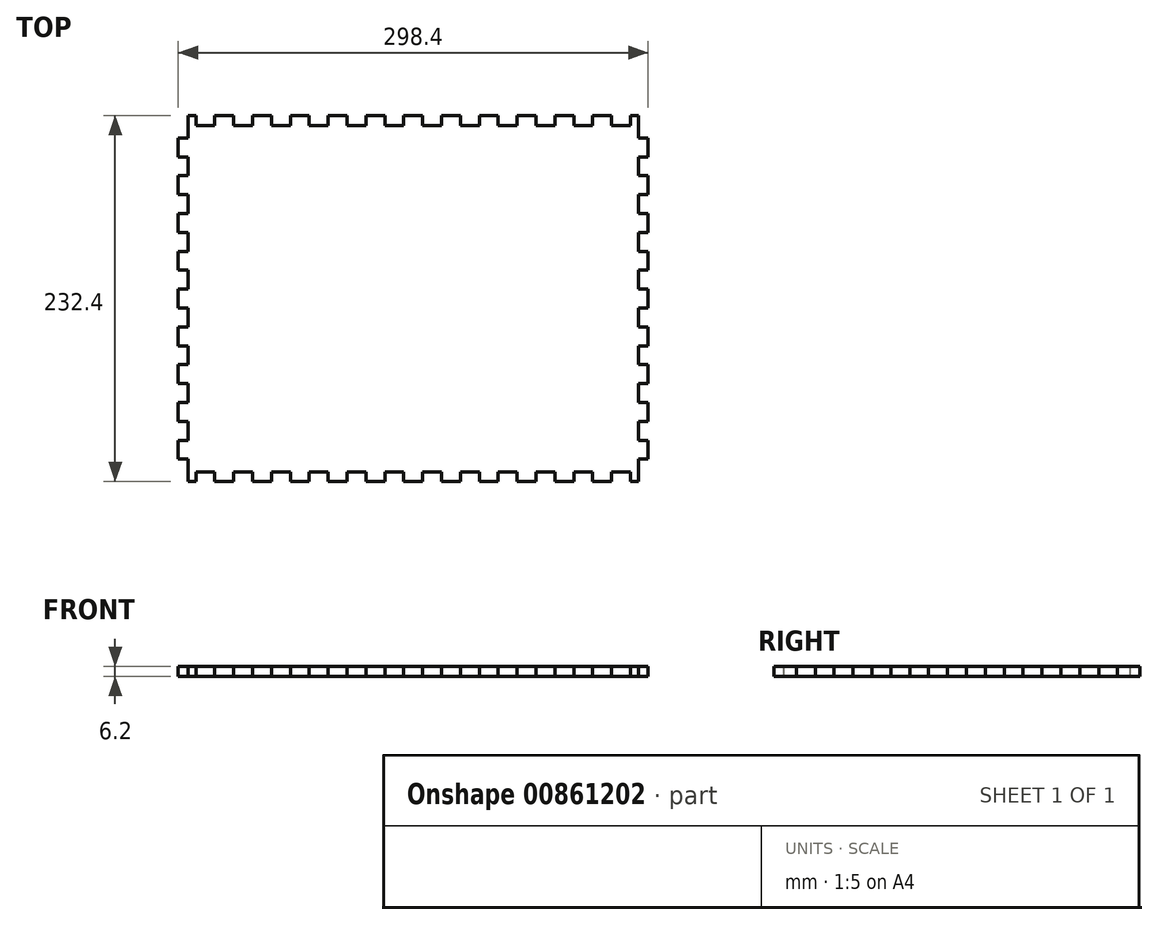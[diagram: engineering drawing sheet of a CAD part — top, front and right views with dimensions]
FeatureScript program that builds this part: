
annotation { "Feature Type Name" : "Feature", "Feature Type Description" : "" }
export const myFeature = defineFeature(function(context is Context, id is Id, definition is map)
    precondition{}
    {
        {
            var Q0;
            Q0=qCreatedBy(makeId("Top.planeOp"),FACE);
            var sketch = newSketch(context, id + "F0", { "sketchPlane" : qUnion([Q0])});
            skLineSegment(sketch, "E0.bottom", {"start": v(143, 110) * mm, "end": v(-143, 110) * mm});
            skLineSegment(sketch, "E0.top", {"start": v(143, -110) * mm, "end": v(-143, -110) * mm});
            skLineSegment(sketch, "E0.left", {"start": v(143, 110) * mm, "end": v(143, -110) * mm});
            skLineSegment(sketch, "E0.right", {"start": v(-143, 110) * mm, "end": v(-143, -110) * mm});
            skPoint(sketch, "E0.middle", {"position": v(0, 0) * mm});
            skSolve(sketch);
        }
        {
            var Q0;
            Q0 = qSketchRegion(id + "F0", true);
            extrude(context, id + "F1", {"entities" : qUnion([Q0]), "depth" : 6.2 * mm, "offsetDistance" : 25 * mm});
        }
        {
            var Q0;
            Q0=makeQuery(id+"F1.opExtrude","CAP_FACE",FACE,{"disambiguationData":[OSD([sQuery(id+"F0.wireOp",EDGE,"E0.bottom"),sQuery(id+"F0.wireOp",EDGE,"E0.top"),sQuery(id+"F0.wireOp",EDGE,"E0.left"),sQuery(id+"F0.wireOp",EDGE,"E0.right")])],"isStart":false});
            var sketch = newSketch(context, id + "F2", { "sketchPlane" : qUnion([Q0])});
            skLineSegment(sketch, "E1", {"start": v(0, 110) * mm, "end": v(0, 116.2) * mm, "construction": true});
            skLineSegment(sketch, "E2.bottom", {"start": v(6, 116.2) * mm, "end": v(-6, 116.2) * mm});
            skLineSegment(sketch, "E2.top", {"start": v(6, 110) * mm, "end": v(-6, 110) * mm});
            skLineSegment(sketch, "E2.left", {"start": v(6, 116.2) * mm, "end": v(6, 110) * mm});
            skLineSegment(sketch, "E2.right", {"start": v(-6, 116.2) * mm, "end": v(-6, 110) * mm});
            skPoint(sketch, "E2.middle", {"position": v(0, 113.1) * mm});
            skLineSegment(sketch, "E3.1.0.0", {"start": v(30, 116.2) * mm, "end": v(18, 116.2) * mm});
            skLineSegment(sketch, "E3.1.0.1", {"start": v(30, 116.2) * mm, "end": v(30, 110) * mm});
            skLineSegment(sketch, "E3.1.0.2", {"start": v(18, 116.2) * mm, "end": v(18, 110) * mm});
            skLineSegment(sketch, "E3.1.0.3", {"start": v(30, 110) * mm, "end": v(18, 110) * mm});
            skLineSegment(sketch, "E3.2.0.0", {"start": v(54, 116.2) * mm, "end": v(42, 116.2) * mm});
            skLineSegment(sketch, "E3.2.0.1", {"start": v(54, 116.2) * mm, "end": v(54, 110) * mm});
            skLineSegment(sketch, "E3.2.0.2", {"start": v(42, 116.2) * mm, "end": v(42, 110) * mm});
            skLineSegment(sketch, "E3.2.0.3", {"start": v(54, 110) * mm, "end": v(42, 110) * mm});
            skLineSegment(sketch, "E3.3.0.0", {"start": v(78, 116.2) * mm, "end": v(66, 116.2) * mm});
            skLineSegment(sketch, "E3.3.0.1", {"start": v(78, 116.2) * mm, "end": v(78, 110) * mm});
            skLineSegment(sketch, "E3.3.0.2", {"start": v(66, 116.2) * mm, "end": v(66, 110) * mm});
            skLineSegment(sketch, "E3.3.0.3", {"start": v(78, 110) * mm, "end": v(66, 110) * mm});
            skLineSegment(sketch, "E3.4.0.0", {"start": v(102, 116.2) * mm, "end": v(90, 116.2) * mm});
            skLineSegment(sketch, "E3.4.0.1", {"start": v(102, 116.2) * mm, "end": v(102, 110) * mm});
            skLineSegment(sketch, "E3.4.0.2", {"start": v(90, 116.2) * mm, "end": v(90, 110) * mm});
            skLineSegment(sketch, "E3.4.0.3", {"start": v(102, 110) * mm, "end": v(90, 110) * mm});
            skLineSegment(sketch, "E3.5.0.0", {"start": v(126, 116.2) * mm, "end": v(114, 116.2) * mm});
            skLineSegment(sketch, "E3.5.0.1", {"start": v(126, 116.2) * mm, "end": v(126, 110) * mm});
            skLineSegment(sketch, "E3.5.0.2", {"start": v(114, 116.2) * mm, "end": v(114, 110) * mm});
            skLineSegment(sketch, "E3.5.0.3", {"start": v(126, 110) * mm, "end": v(114, 110) * mm});
            skLineSegment(sketch, "E3.6.0.0", {"start": v(143, 116.2) * mm, "end": v(138, 116.2) * mm});
            skLineSegment(sketch, "E3.6.0.2", {"start": v(138, 116.2) * mm, "end": v(138, 110) * mm});
            skLineSegment(sketch, "E3.6.0.3", {"start": v(143, 110) * mm, "end": v(138, 110) * mm});
            skLineSegment(sketch, "E3.direction1", {"start": v(-6, 116.2) * mm, "end": v(18, 116.2) * mm, "construction": true});
            skLineSegment(sketch, "E4", {"start": v(143, 110) * mm, "end": v(143, 116.2) * mm});
            skPoint(sketch, "E5.orphan", {"position": v(150, 110) * mm});
            skLineSegment(sketch, "E6.MirrorCS", {"start": v(-102, 110) * mm, "end": v(-90, 110) * mm});
            skLineSegment(sketch, "E7.MirrorCS", {"start": v(-143, 116.2) * mm, "end": v(-138, 116.2) * mm});
            skLineSegment(sketch, "E8.MirrorCS", {"start": v(-138, 116.2) * mm, "end": v(-138, 110) * mm});
            skLineSegment(sketch, "E9.MirrorCS", {"start": v(-30, 116.2) * mm, "end": v(-30, 110) * mm});
            skLineSegment(sketch, "E10.MirrorCS", {"start": v(-66, 116.2) * mm, "end": v(-66, 110) * mm});
            skLineSegment(sketch, "E11.MirrorCS", {"start": v(-126, 116.2) * mm, "end": v(-126, 110) * mm});
            skLineSegment(sketch, "E12.MirrorCS", {"start": v(-54, 110) * mm, "end": v(-42, 110) * mm});
            skLineSegment(sketch, "E13.MirrorCS", {"start": v(-143, 110) * mm, "end": v(-143, 116.2) * mm});
            skLineSegment(sketch, "E14.MirrorCS", {"start": v(-54, 116.2) * mm, "end": v(-54, 110) * mm});
            skLineSegment(sketch, "E15.MirrorCS", {"start": v(-114, 116.2) * mm, "end": v(-114, 110) * mm});
            skLineSegment(sketch, "E16.MirrorCS", {"start": v(-102, 116.2) * mm, "end": v(-90, 116.2) * mm});
            skLineSegment(sketch, "E17.MirrorCS", {"start": v(-102, 116.2) * mm, "end": v(-102, 110) * mm});
            skLineSegment(sketch, "E18.MirrorCS", {"start": v(-42, 116.2) * mm, "end": v(-42, 110) * mm});
            skLineSegment(sketch, "E19.MirrorCS", {"start": v(-54, 116.2) * mm, "end": v(-42, 116.2) * mm});
            skLineSegment(sketch, "E20.MirrorCS", {"start": v(-143, 110) * mm, "end": v(-138, 110) * mm});
            skLineSegment(sketch, "E21.MirrorCS", {"start": v(-90, 116.2) * mm, "end": v(-90, 110) * mm});
            skLineSegment(sketch, "E22.MirrorCS", {"start": v(-78, 116.2) * mm, "end": v(-78, 110) * mm});
            skLineSegment(sketch, "E23.MirrorCS", {"start": v(-78, 110) * mm, "end": v(-66, 110) * mm});
            skLineSegment(sketch, "E24.MirrorCS", {"start": v(-126, 116.2) * mm, "end": v(-114, 116.2) * mm});
            skLineSegment(sketch, "E25.MirrorCS", {"start": v(-78, 116.2) * mm, "end": v(-66, 116.2) * mm});
            skLineSegment(sketch, "E26.MirrorCS", {"start": v(-126, 110) * mm, "end": v(-114, 110) * mm});
            skLineSegment(sketch, "E27.MirrorCS", {"start": v(-30, 110) * mm, "end": v(-18, 110) * mm});
            skPoint(sketch, "E28.MirrorP", {"position": v(-150, 110) * mm});
            skLineSegment(sketch, "E29.MirrorCS", {"start": v(-30, 116.2) * mm, "end": v(-18, 116.2) * mm});
            skLineSegment(sketch, "E30.MirrorCS", {"start": v(-18, 116.2) * mm, "end": v(-18, 110) * mm});
            skLineSegment(sketch, "E31.MirrorCS", {"start": v(6, -116.2) * mm, "end": v(-6, -116.2) * mm});
            skLineSegment(sketch, "E32.MirrorCS", {"start": v(-143, -116.2) * mm, "end": v(-138, -116.2) * mm});
            skLineSegment(sketch, "E33.MirrorCS", {"start": v(143, -110) * mm, "end": v(138, -110) * mm});
            skLineSegment(sketch, "E34.MirrorCS", {"start": v(-30, -116.2) * mm, "end": v(-30, -110) * mm});
            skLineSegment(sketch, "E35.MirrorCS", {"start": v(-143, -110) * mm, "end": v(-143, -116.2) * mm});
            skLineSegment(sketch, "E36.MirrorCS", {"start": v(-6, -116.2) * mm, "end": v(18, -116.2) * mm, "construction": true});
            skLineSegment(sketch, "E37.MirrorCS", {"start": v(-42, -116.2) * mm, "end": v(-42, -110) * mm});
            skLineSegment(sketch, "E38.MirrorCS", {"start": v(143, -110) * mm, "end": v(143, -116.2) * mm});
            skLineSegment(sketch, "E39.MirrorCS", {"start": v(-143, -110) * mm, "end": v(-138, -110) * mm});
            skLineSegment(sketch, "E40.MirrorCS", {"start": v(18, -116.2) * mm, "end": v(18, -110) * mm});
            skLineSegment(sketch, "E41.MirrorCS", {"start": v(-138, -116.2) * mm, "end": v(-138, -110) * mm});
            skLineSegment(sketch, "E42.MirrorCS", {"start": v(0, -110) * mm, "end": v(0, -116.2) * mm, "construction": true});
            skLineSegment(sketch, "E43.MirrorCS", {"start": v(-6, -116.2) * mm, "end": v(-6, -110) * mm});
            skLineSegment(sketch, "E44.MirrorCS", {"start": v(-54, -116.2) * mm, "end": v(-42, -116.2) * mm});
            skLineSegment(sketch, "E45.MirrorCS", {"start": v(6, -116.2) * mm, "end": v(6, -110) * mm});
            skLineSegment(sketch, "E46.MirrorCS", {"start": v(138, -116.2) * mm, "end": v(138, -110) * mm});
            skLineSegment(sketch, "E47.MirrorCS", {"start": v(6, -110) * mm, "end": v(-6, -110) * mm});
            skLineSegment(sketch, "E48.MirrorCS", {"start": v(143, -116.2) * mm, "end": v(138, -116.2) * mm});
            skLineSegment(sketch, "E49.MirrorCS", {"start": v(-30, -116.2) * mm, "end": v(-18, -116.2) * mm});
            skLineSegment(sketch, "E50.MirrorCS", {"start": v(-126, -116.2) * mm, "end": v(-126, -110) * mm});
            skLineSegment(sketch, "E51.MirrorCS", {"start": v(-102, -116.2) * mm, "end": v(-90, -116.2) * mm});
            skLineSegment(sketch, "E52.MirrorCS", {"start": v(126, -116.2) * mm, "end": v(114, -116.2) * mm});
            skLineSegment(sketch, "E53.MirrorCS", {"start": v(102, -116.2) * mm, "end": v(90, -116.2) * mm});
            skLineSegment(sketch, "E54.MirrorCS", {"start": v(126, -116.2) * mm, "end": v(126, -110) * mm});
            skLineSegment(sketch, "E55.MirrorCS", {"start": v(126, -110) * mm, "end": v(114, -110) * mm});
            skLineSegment(sketch, "E56.MirrorCS", {"start": v(78, -116.2) * mm, "end": v(66, -116.2) * mm});
            skLineSegment(sketch, "E57.MirrorCS", {"start": v(30, -110) * mm, "end": v(18, -110) * mm});
            skLineSegment(sketch, "E58.MirrorCS", {"start": v(-126, -116.2) * mm, "end": v(-114, -116.2) * mm});
            skLineSegment(sketch, "E59.MirrorCS", {"start": v(-18, -116.2) * mm, "end": v(-18, -110) * mm});
            skLineSegment(sketch, "E60.MirrorCS", {"start": v(54, -116.2) * mm, "end": v(42, -116.2) * mm});
            skLineSegment(sketch, "E61.MirrorCS", {"start": v(30, -116.2) * mm, "end": v(18, -116.2) * mm});
            skLineSegment(sketch, "E62.MirrorCS", {"start": v(54, -116.2) * mm, "end": v(54, -110) * mm});
            skLineSegment(sketch, "E63.MirrorCS", {"start": v(54, -110) * mm, "end": v(42, -110) * mm});
            skLineSegment(sketch, "E64.MirrorCS", {"start": v(-78, -116.2) * mm, "end": v(-66, -116.2) * mm});
            skLineSegment(sketch, "E65.MirrorCS", {"start": v(-30, -110) * mm, "end": v(-18, -110) * mm});
            skLineSegment(sketch, "E66.MirrorCS", {"start": v(-102, -110) * mm, "end": v(-90, -110) * mm});
            skLineSegment(sketch, "E67.MirrorCS", {"start": v(-102, -116.2) * mm, "end": v(-102, -110) * mm});
            skLineSegment(sketch, "E68.MirrorCS", {"start": v(90, -116.2) * mm, "end": v(90, -110) * mm});
            skLineSegment(sketch, "E69.MirrorCS", {"start": v(78, -110) * mm, "end": v(66, -110) * mm});
            skLineSegment(sketch, "E70.MirrorCS", {"start": v(78, -116.2) * mm, "end": v(78, -110) * mm});
            skLineSegment(sketch, "E71.MirrorCS", {"start": v(66, -116.2) * mm, "end": v(66, -110) * mm});
            skLineSegment(sketch, "E72.MirrorCS", {"start": v(102, -110) * mm, "end": v(90, -110) * mm});
            skLineSegment(sketch, "E73.MirrorCS", {"start": v(-114, -116.2) * mm, "end": v(-114, -110) * mm});
            skLineSegment(sketch, "E74.MirrorCS", {"start": v(-126, -110) * mm, "end": v(-114, -110) * mm});
            skLineSegment(sketch, "E75.MirrorCS", {"start": v(-90, -116.2) * mm, "end": v(-90, -110) * mm});
            skLineSegment(sketch, "E76.MirrorCS", {"start": v(-78, -110) * mm, "end": v(-66, -110) * mm});
            skLineSegment(sketch, "E77.MirrorCS", {"start": v(-54, -110) * mm, "end": v(-42, -110) * mm});
            skLineSegment(sketch, "E78.MirrorCS", {"start": v(114, -116.2) * mm, "end": v(114, -110) * mm});
            skLineSegment(sketch, "E79.MirrorCS", {"start": v(-54, -116.2) * mm, "end": v(-54, -110) * mm});
            skLineSegment(sketch, "E80.MirrorCS", {"start": v(-78, -116.2) * mm, "end": v(-78, -110) * mm});
            skLineSegment(sketch, "E81.MirrorCS", {"start": v(42, -116.2) * mm, "end": v(42, -110) * mm});
            skLineSegment(sketch, "E82.MirrorCS", {"start": v(102, -116.2) * mm, "end": v(102, -110) * mm});
            skLineSegment(sketch, "E83.MirrorCS", {"start": v(-66, -116.2) * mm, "end": v(-66, -110) * mm});
            skLineSegment(sketch, "E84.MirrorCS", {"start": v(30, -116.2) * mm, "end": v(30, -110) * mm});
            skPoint(sketch, "E85.MirrorP", {"position": v(-150, -110) * mm});
            skPoint(sketch, "E86.MirrorP", {"position": v(0, -113.1) * mm});
            skPoint(sketch, "E87.MirrorP", {"position": v(150, -110) * mm});
            skSolve(sketch);
        }
        {
            var Q0;
            Q0=makeQuery(id+"F2.imprint","IMPRINT",FACE,{"disambiguationData":[TD([[makeQuery(id+"F2.imprint","IMPRINT",EDGE,{"derivedFrom":sQuery(id+"F2.wireOp",EDGE,"E3.6.0.0")}),1.0]])]});
            var Q1;
            Q1=makeQuery(id+"F2.imprint","IMPRINT",FACE,{"disambiguationData":[TD([[makeQuery(id+"F2.imprint","IMPRINT",EDGE,{"derivedFrom":sQuery(id+"F2.wireOp",EDGE,"E3.5.0.0")}),1.0]])]});
            var Q2;
            Q2=makeQuery(id+"F2.imprint","IMPRINT",FACE,{"disambiguationData":[TD([[makeQuery(id+"F2.imprint","IMPRINT",EDGE,{"derivedFrom":sQuery(id+"F2.wireOp",EDGE,"E3.4.0.0")}),1.0]])]});
            var Q3;
            Q3=makeQuery(id+"F2.imprint","IMPRINT",FACE,{"disambiguationData":[TD([[makeQuery(id+"F2.imprint","IMPRINT",EDGE,{"derivedFrom":sQuery(id+"F2.wireOp",EDGE,"E3.3.0.0")}),1.0]])]});
            var Q4;
            Q4=makeQuery(id+"F2.imprint","IMPRINT",FACE,{"disambiguationData":[TD([[makeQuery(id+"F2.imprint","IMPRINT",EDGE,{"derivedFrom":sQuery(id+"F2.wireOp",EDGE,"E3.2.0.0")}),1.0]])]});
            var Q5;
            Q5=makeQuery(id+"F2.imprint","IMPRINT",FACE,{"disambiguationData":[TD([[makeQuery(id+"F2.imprint","IMPRINT",EDGE,{"derivedFrom":sQuery(id+"F2.wireOp",EDGE,"E3.1.0.0")}),1.0]])]});
            var Q6;
            Q6=makeQuery(id+"F2.imprint","IMPRINT",FACE,{"disambiguationData":[TD([[makeQuery(id+"F2.imprint","IMPRINT",EDGE,{"derivedFrom":sQuery(id+"F2.wireOp",EDGE,"E2.bottom")}),1.0]])]});
            var Q7;
            Q7=makeQuery(id+"F2.imprint","IMPRINT",FACE,{"disambiguationData":[TD([[makeQuery(id+"F2.imprint","IMPRINT",EDGE,{"derivedFrom":sQuery(id+"F2.wireOp",EDGE,"E9.MirrorCS")}),1.0]])]});
            var Q8;
            Q8=makeQuery(id+"F2.imprint","IMPRINT",FACE,{"disambiguationData":[TD([[makeQuery(id+"F2.imprint","IMPRINT",EDGE,{"derivedFrom":sQuery(id+"F2.wireOp",EDGE,"E12.MirrorCS")}),-1.0]])]});
            var Q9;
            Q9=makeQuery(id+"F2.imprint","IMPRINT",FACE,{"disambiguationData":[TD([[makeQuery(id+"F2.imprint","IMPRINT",EDGE,{"derivedFrom":sQuery(id+"F2.wireOp",EDGE,"E10.MirrorCS")}),-1.0]])]});
            var Q10;
            Q10=makeQuery(id+"F2.imprint","IMPRINT",FACE,{"disambiguationData":[TD([[makeQuery(id+"F2.imprint","IMPRINT",EDGE,{"derivedFrom":sQuery(id+"F2.wireOp",EDGE,"E6.MirrorCS")}),-1.0]])]});
            var Q11;
            Q11=makeQuery(id+"F2.imprint","IMPRINT",FACE,{"disambiguationData":[TD([[makeQuery(id+"F2.imprint","IMPRINT",EDGE,{"derivedFrom":sQuery(id+"F2.wireOp",EDGE,"E11.MirrorCS")}),1.0]])]});
            var Q12;
            Q12=makeQuery(id+"F2.imprint","IMPRINT",FACE,{"disambiguationData":[TD([[makeQuery(id+"F2.imprint","IMPRINT",EDGE,{"derivedFrom":sQuery(id+"F2.wireOp",EDGE,"E7.MirrorCS")}),-1.0]])]});
            var Q13;
            Q13=makeQuery(id+"F2.imprint","IMPRINT",FACE,{"disambiguationData":[TD([[makeQuery(id+"F2.imprint","IMPRINT",EDGE,{"derivedFrom":sQuery(id+"F2.wireOp",EDGE,"E32.MirrorCS")}),1.0]])]});
            var Q14;
            Q14=makeQuery(id+"F2.imprint","IMPRINT",FACE,{"disambiguationData":[TD([[makeQuery(id+"F2.imprint","IMPRINT",EDGE,{"derivedFrom":sQuery(id+"F2.wireOp",EDGE,"E50.MirrorCS")}),-1.0]])]});
            var Q15;
            Q15=makeQuery(id+"F2.imprint","IMPRINT",FACE,{"disambiguationData":[TD([[makeQuery(id+"F2.imprint","IMPRINT",EDGE,{"derivedFrom":sQuery(id+"F2.wireOp",EDGE,"E51.MirrorCS")}),1.0]])]});
            var Q16;
            Q16=makeQuery(id+"F2.imprint","IMPRINT",FACE,{"disambiguationData":[TD([[makeQuery(id+"F2.imprint","IMPRINT",EDGE,{"derivedFrom":sQuery(id+"F2.wireOp",EDGE,"E64.MirrorCS")}),1.0]])]});
            var Q17;
            Q17=makeQuery(id+"F2.imprint","IMPRINT",FACE,{"disambiguationData":[TD([[makeQuery(id+"F2.imprint","IMPRINT",EDGE,{"derivedFrom":sQuery(id+"F2.wireOp",EDGE,"E37.MirrorCS")}),1.0]])]});
            var Q18;
            Q18=makeQuery(id+"F2.imprint","IMPRINT",FACE,{"disambiguationData":[TD([[makeQuery(id+"F2.imprint","IMPRINT",EDGE,{"derivedFrom":sQuery(id+"F2.wireOp",EDGE,"E34.MirrorCS")}),-1.0]])]});
            var Q19;
            Q19=makeQuery(id+"F2.imprint","IMPRINT",FACE,{"disambiguationData":[TD([[makeQuery(id+"F2.imprint","IMPRINT",EDGE,{"derivedFrom":sQuery(id+"F2.wireOp",EDGE,"E31.MirrorCS")}),-1.0]])]});
            var Q20;
            Q20=makeQuery(id+"F2.imprint","IMPRINT",FACE,{"disambiguationData":[TD([[makeQuery(id+"F2.imprint","IMPRINT",EDGE,{"derivedFrom":sQuery(id+"F2.wireOp",EDGE,"E40.MirrorCS")}),-1.0]])]});
            var Q21;
            Q21=makeQuery(id+"F2.imprint","IMPRINT",FACE,{"disambiguationData":[TD([[makeQuery(id+"F2.imprint","IMPRINT",EDGE,{"derivedFrom":sQuery(id+"F2.wireOp",EDGE,"E60.MirrorCS")}),-1.0]])]});
            var Q22;
            Q22=makeQuery(id+"F2.imprint","IMPRINT",FACE,{"disambiguationData":[TD([[makeQuery(id+"F2.imprint","IMPRINT",EDGE,{"derivedFrom":sQuery(id+"F2.wireOp",EDGE,"E56.MirrorCS")}),-1.0]])]});
            var Q23;
            Q23=makeQuery(id+"F2.imprint","IMPRINT",FACE,{"disambiguationData":[TD([[makeQuery(id+"F2.imprint","IMPRINT",EDGE,{"derivedFrom":sQuery(id+"F2.wireOp",EDGE,"E53.MirrorCS")}),-1.0]])]});
            var Q24;
            Q24=makeQuery(id+"F2.imprint","IMPRINT",FACE,{"disambiguationData":[TD([[makeQuery(id+"F2.imprint","IMPRINT",EDGE,{"derivedFrom":sQuery(id+"F2.wireOp",EDGE,"E52.MirrorCS")}),-1.0]])]});
            var Q25;
            Q25=makeQuery(id+"F2.imprint","IMPRINT",FACE,{"disambiguationData":[TD([[makeQuery(id+"F2.imprint","IMPRINT",EDGE,{"derivedFrom":sQuery(id+"F2.wireOp",EDGE,"E33.MirrorCS")}),1.0]])]});
            var Q26;
            Q26=makeQuery(id+"F1.opExtrude","CAP_FACE",FACE,{"disambiguationData":[OSD([sQuery(id+"F0.wireOp",EDGE,"E0.bottom"),sQuery(id+"F0.wireOp",EDGE,"E0.top"),sQuery(id+"F0.wireOp",EDGE,"E0.left"),sQuery(id+"F0.wireOp",EDGE,"E0.right")])],"isStart":true});
            extrude(context, id + "F3", {"entities" : qUnion([Q0, Q1, Q2, Q3, Q4, Q5, Q6, Q7, Q8, Q9, Q10, Q11, Q12, Q13, Q14, Q15, Q16, Q17, Q18, Q19, Q20, Q21, Q22, Q23, Q24, Q25]), "operationType" : NewBodyOperationType.ADD, "endBound" : BoundingType.UP_TO_SURFACE, "oppositeDirection" : true, "depth" : 25 * mm, "endBoundEntityFace" : qUnion([Q26]), "offsetDistance" : 25 * mm});
        }
        {
            var Q0;
            Q0=makeQuery(id+"F3.boolean.opBoolean","MERGE",FACE,{"derivedFrom":[makeQuery(id+"F1.opExtrude","CAP_FACE",FACE,{"disambiguationData":[OSD([sQuery(id+"F0.wireOp",EDGE,"E0.bottom"),sQuery(id+"F0.wireOp",EDGE,"E0.top"),sQuery(id+"F0.wireOp",EDGE,"E0.left"),sQuery(id+"F0.wireOp",EDGE,"E0.right")])],"isStart":false}),makeQuery(id+"F3.opExtrude","CAP_FACE",FACE,{"disambiguationData":[OSD([sQuery(id+"F2.wireOp",EDGE,"E2.bottom"),sQuery(id+"F2.wireOp",EDGE,"E2.top"),sQuery(id+"F2.wireOp",EDGE,"E2.left"),sQuery(id+"F2.wireOp",EDGE,"E2.right")])],"isStart":true}),makeQuery(id+"F3.opExtrude","CAP_FACE",FACE,{"disambiguationData":[OSD([sQuery(id+"F2.wireOp",EDGE,"E3.1.0.0"),sQuery(id+"F2.wireOp",EDGE,"E3.1.0.1"),sQuery(id+"F2.wireOp",EDGE,"E3.1.0.2"),sQuery(id+"F2.wireOp",EDGE,"E3.1.0.3")])],"isStart":true}),makeQuery(id+"F3.opExtrude","CAP_FACE",FACE,{"disambiguationData":[OSD([sQuery(id+"F2.wireOp",EDGE,"E3.2.0.0"),sQuery(id+"F2.wireOp",EDGE,"E3.2.0.1"),sQuery(id+"F2.wireOp",EDGE,"E3.2.0.2"),sQuery(id+"F2.wireOp",EDGE,"E3.2.0.3")])],"isStart":true}),makeQuery(id+"F3.opExtrude","CAP_FACE",FACE,{"disambiguationData":[OSD([sQuery(id+"F2.wireOp",EDGE,"E3.3.0.0"),sQuery(id+"F2.wireOp",EDGE,"E3.3.0.1"),sQuery(id+"F2.wireOp",EDGE,"E3.3.0.2"),sQuery(id+"F2.wireOp",EDGE,"E3.3.0.3")])],"isStart":true}),makeQuery(id+"F3.opExtrude","CAP_FACE",FACE,{"disambiguationData":[OSD([sQuery(id+"F2.wireOp",EDGE,"E3.4.0.0"),sQuery(id+"F2.wireOp",EDGE,"E3.4.0.1"),sQuery(id+"F2.wireOp",EDGE,"E3.4.0.2"),sQuery(id+"F2.wireOp",EDGE,"E3.4.0.3")])],"isStart":true}),makeQuery(id+"F3.opExtrude","CAP_FACE",FACE,{"disambiguationData":[OSD([sQuery(id+"F2.wireOp",EDGE,"E3.5.0.0"),sQuery(id+"F2.wireOp",EDGE,"E3.5.0.1"),sQuery(id+"F2.wireOp",EDGE,"E3.5.0.2"),sQuery(id+"F2.wireOp",EDGE,"E3.5.0.3")])],"isStart":true}),makeQuery(id+"F3.opExtrude","CAP_FACE",FACE,{"disambiguationData":[OSD([sQuery(id+"F2.wireOp",EDGE,"E3.6.0.0"),sQuery(id+"F2.wireOp",EDGE,"E3.6.0.2"),sQuery(id+"F2.wireOp",EDGE,"E3.6.0.3"),sQuery(id+"F2.wireOp",EDGE,"E4")])],"isStart":true}),makeQuery(id+"F3.opExtrude","CAP_FACE",FACE,{"disambiguationData":[OSD([sQuery(id+"F2.wireOp",EDGE,"E6.MirrorCS"),sQuery(id+"F2.wireOp",EDGE,"E16.MirrorCS"),sQuery(id+"F2.wireOp",EDGE,"E17.MirrorCS"),sQuery(id+"F2.wireOp",EDGE,"E21.MirrorCS")])],"isStart":true}),makeQuery(id+"F3.opExtrude","CAP_FACE",FACE,{"disambiguationData":[OSD([sQuery(id+"F2.wireOp",EDGE,"E7.MirrorCS"),sQuery(id+"F2.wireOp",EDGE,"E8.MirrorCS"),sQuery(id+"F2.wireOp",EDGE,"E13.MirrorCS"),sQuery(id+"F2.wireOp",EDGE,"E20.MirrorCS")])],"isStart":true}),makeQuery(id+"F3.opExtrude","CAP_FACE",FACE,{"disambiguationData":[OSD([sQuery(id+"F2.wireOp",EDGE,"E9.MirrorCS"),sQuery(id+"F2.wireOp",EDGE,"E27.MirrorCS"),sQuery(id+"F2.wireOp",EDGE,"E29.MirrorCS"),sQuery(id+"F2.wireOp",EDGE,"E30.MirrorCS")])],"isStart":true}),makeQuery(id+"F3.opExtrude","CAP_FACE",FACE,{"disambiguationData":[OSD([sQuery(id+"F2.wireOp",EDGE,"E10.MirrorCS"),sQuery(id+"F2.wireOp",EDGE,"E22.MirrorCS"),sQuery(id+"F2.wireOp",EDGE,"E23.MirrorCS"),sQuery(id+"F2.wireOp",EDGE,"E25.MirrorCS")])],"isStart":true}),makeQuery(id+"F3.opExtrude","CAP_FACE",FACE,{"disambiguationData":[OSD([sQuery(id+"F2.wireOp",EDGE,"E11.MirrorCS"),sQuery(id+"F2.wireOp",EDGE,"E15.MirrorCS"),sQuery(id+"F2.wireOp",EDGE,"E24.MirrorCS"),sQuery(id+"F2.wireOp",EDGE,"E26.MirrorCS")])],"isStart":true}),makeQuery(id+"F3.opExtrude","CAP_FACE",FACE,{"disambiguationData":[OSD([sQuery(id+"F2.wireOp",EDGE,"E12.MirrorCS"),sQuery(id+"F2.wireOp",EDGE,"E14.MirrorCS"),sQuery(id+"F2.wireOp",EDGE,"E18.MirrorCS"),sQuery(id+"F2.wireOp",EDGE,"E19.MirrorCS")])],"isStart":true})]});
            var sketch = newSketch(context, id + "F4", { "sketchPlane" : qUnion([Q0])});
            skLineSegment(sketch, "E88", {"start": v(-138, 110) * mm, "end": v(143, 110) * mm, "construction": true});
            skLineSegment(sketch, "E89", {"start": v(0, 0) * mm, "end": v(143, 0) * mm, "construction": true});
            skLineSegment(sketch, "E90", {"start": v(143, 0) * mm, "end": v(149.2, 0) * mm, "construction": true});
            skLineSegment(sketch, "E91.bottom", {"start": v(149.2, 6) * mm, "end": v(143, 6) * mm});
            skLineSegment(sketch, "E91.top", {"start": v(149.2, -6) * mm, "end": v(143, -6) * mm});
            skLineSegment(sketch, "E91.left", {"start": v(149.2, 6) * mm, "end": v(149.2, -6) * mm});
            skLineSegment(sketch, "E91.right", {"start": v(143, 6) * mm, "end": v(143, -6) * mm});
            skPoint(sketch, "E91.middle", {"position": v(146.1, 0) * mm});
            skLineSegment(sketch, "E92.0.1.0", {"start": v(149.2, 30) * mm, "end": v(143, 30) * mm});
            skLineSegment(sketch, "E92.0.1.1", {"start": v(143, 30) * mm, "end": v(143, 18) * mm});
            skLineSegment(sketch, "E92.0.1.2", {"start": v(149.2, 30) * mm, "end": v(149.2, 18) * mm});
            skLineSegment(sketch, "E92.0.1.3", {"start": v(149.2, 18) * mm, "end": v(143, 18) * mm});
            skLineSegment(sketch, "E92.0.2.0", {"start": v(149.2, 54) * mm, "end": v(143, 54) * mm});
            skLineSegment(sketch, "E92.0.2.1", {"start": v(143, 54) * mm, "end": v(143, 42) * mm});
            skLineSegment(sketch, "E92.0.2.2", {"start": v(149.2, 54) * mm, "end": v(149.2, 42) * mm});
            skLineSegment(sketch, "E92.0.2.3", {"start": v(149.2, 42) * mm, "end": v(143, 42) * mm});
            skLineSegment(sketch, "E92.0.3.0", {"start": v(149.2, 78) * mm, "end": v(143, 78) * mm});
            skLineSegment(sketch, "E92.0.3.1", {"start": v(143, 78) * mm, "end": v(143, 66) * mm});
            skLineSegment(sketch, "E92.0.3.2", {"start": v(149.2, 78) * mm, "end": v(149.2, 66) * mm});
            skLineSegment(sketch, "E92.0.3.3", {"start": v(149.2, 66) * mm, "end": v(143, 66) * mm});
            skLineSegment(sketch, "E92.0.4.0", {"start": v(149.2, 102) * mm, "end": v(143, 102) * mm});
            skLineSegment(sketch, "E92.0.4.1", {"start": v(143, 102) * mm, "end": v(143, 90) * mm});
            skLineSegment(sketch, "E92.0.4.2", {"start": v(149.2, 102) * mm, "end": v(149.2, 90) * mm});
            skLineSegment(sketch, "E92.0.4.3", {"start": v(149.2, 90) * mm, "end": v(143, 90) * mm});
            skLineSegment(sketch, "E92.direction1", {"start": v(143, 6) * mm, "end": v(168, 6) * mm, "construction": true});
            skLineSegment(sketch, "E92.direction2", {"start": v(143, 6) * mm, "end": v(143, 30) * mm, "construction": true});
            skLineSegment(sketch, "E93.MirrorCS", {"start": v(143, -30) * mm, "end": v(143, -18) * mm});
            skLineSegment(sketch, "E94.MirrorCS", {"start": v(149.2, -78) * mm, "end": v(149.2, -66) * mm});
            skLineSegment(sketch, "E95.MirrorCS", {"start": v(149.2, -66) * mm, "end": v(143, -66) * mm});
            skLineSegment(sketch, "E96.MirrorCS", {"start": v(149.2, -102) * mm, "end": v(143, -102) * mm});
            skLineSegment(sketch, "E97.MirrorCS", {"start": v(143, -102) * mm, "end": v(143, -90) * mm});
            skLineSegment(sketch, "E98.MirrorCS", {"start": v(149.2, -102) * mm, "end": v(149.2, -90) * mm});
            skLineSegment(sketch, "E99.MirrorCS", {"start": v(149.2, -90) * mm, "end": v(143, -90) * mm});
            skLineSegment(sketch, "E100.MirrorCS", {"start": v(143, -6) * mm, "end": v(143, -30) * mm, "construction": true});
            skLineSegment(sketch, "E101.MirrorCS", {"start": v(143, -54) * mm, "end": v(143, -42) * mm});
            skLineSegment(sketch, "E102.MirrorCS", {"start": v(149.2, -42) * mm, "end": v(143, -42) * mm});
            skLineSegment(sketch, "E103.MirrorCS", {"start": v(149.2, -54) * mm, "end": v(143, -54) * mm});
            skLineSegment(sketch, "E104.MirrorCS", {"start": v(149.2, -54) * mm, "end": v(149.2, -42) * mm});
            skLineSegment(sketch, "E105.MirrorCS", {"start": v(149.2, -18) * mm, "end": v(143, -18) * mm});
            skLineSegment(sketch, "E106.MirrorCS", {"start": v(143, -78) * mm, "end": v(143, -66) * mm});
            skLineSegment(sketch, "E107.MirrorCS", {"start": v(149.2, -78) * mm, "end": v(143, -78) * mm});
            skLineSegment(sketch, "E108.MirrorCS", {"start": v(149.2, -30) * mm, "end": v(143, -30) * mm});
            skLineSegment(sketch, "E109.MirrorCS", {"start": v(149.2, -30) * mm, "end": v(149.2, -18) * mm});
            skLineSegment(sketch, "E110.MirrorCS", {"start": v(-143, 6) * mm, "end": v(-143, -6) * mm});
            skLineSegment(sketch, "E111.MirrorCS", {"start": v(-149.2, 6) * mm, "end": v(-149.2, -6) * mm});
            skLineSegment(sketch, "E112.MirrorCS", {"start": v(-149.2, -6) * mm, "end": v(-143, -6) * mm});
            skLineSegment(sketch, "E113.MirrorCS", {"start": v(-149.2, 6) * mm, "end": v(-143, 6) * mm});
            skLineSegment(sketch, "E114.MirrorCS", {"start": v(-143, 0) * mm, "end": v(-149.2, 0) * mm, "construction": true});
            skLineSegment(sketch, "E115.MirrorCS", {"start": v(-143, 30) * mm, "end": v(-143, 18) * mm});
            skLineSegment(sketch, "E116.MirrorCS", {"start": v(-149.2, -30) * mm, "end": v(-143, -30) * mm});
            skLineSegment(sketch, "E117.MirrorCS", {"start": v(-143, -30) * mm, "end": v(-143, -18) * mm});
            skLineSegment(sketch, "E118.MirrorCS", {"start": v(-149.2, 30) * mm, "end": v(-143, 30) * mm});
            skLineSegment(sketch, "E119.MirrorCS", {"start": v(-149.2, 78) * mm, "end": v(-149.2, 66) * mm});
            skLineSegment(sketch, "E120.MirrorCS", {"start": v(-143, -54) * mm, "end": v(-143, -42) * mm});
            skLineSegment(sketch, "E121.MirrorCS", {"start": v(-149.2, 66) * mm, "end": v(-143, 66) * mm});
            skLineSegment(sketch, "E122.MirrorCS", {"start": v(-149.2, -42) * mm, "end": v(-143, -42) * mm});
            skLineSegment(sketch, "E123.MirrorCS", {"start": v(-149.2, 102) * mm, "end": v(-143, 102) * mm});
            skLineSegment(sketch, "E124.MirrorCS", {"start": v(-149.2, -54) * mm, "end": v(-143, -54) * mm});
            skLineSegment(sketch, "E125.MirrorCS", {"start": v(-149.2, -90) * mm, "end": v(-143, -90) * mm});
            skLineSegment(sketch, "E126.MirrorCS", {"start": v(-143, 102) * mm, "end": v(-143, 90) * mm});
            skLineSegment(sketch, "E127.MirrorCS", {"start": v(-149.2, -54) * mm, "end": v(-149.2, -42) * mm});
            skLineSegment(sketch, "E128.MirrorCS", {"start": v(-143, -102) * mm, "end": v(-143, -90) * mm});
            skLineSegment(sketch, "E129.MirrorCS", {"start": v(-149.2, 102) * mm, "end": v(-149.2, 90) * mm});
            skLineSegment(sketch, "E130.MirrorCS", {"start": v(-149.2, -18) * mm, "end": v(-143, -18) * mm});
            skLineSegment(sketch, "E131.MirrorCS", {"start": v(-149.2, -102) * mm, "end": v(-149.2, -90) * mm});
            skLineSegment(sketch, "E132.MirrorCS", {"start": v(-143, 78) * mm, "end": v(-143, 66) * mm});
            skLineSegment(sketch, "E133.MirrorCS", {"start": v(-149.2, 18) * mm, "end": v(-143, 18) * mm});
            skLineSegment(sketch, "E134.MirrorCS", {"start": v(-149.2, 42) * mm, "end": v(-143, 42) * mm});
            skLineSegment(sketch, "E135.MirrorCS", {"start": v(-149.2, -102) * mm, "end": v(-143, -102) * mm});
            skLineSegment(sketch, "E136.MirrorCS", {"start": v(-149.2, 30) * mm, "end": v(-149.2, 18) * mm});
            skLineSegment(sketch, "E137.MirrorCS", {"start": v(-149.2, -66) * mm, "end": v(-143, -66) * mm});
            skLineSegment(sketch, "E138.MirrorCS", {"start": v(-149.2, 54) * mm, "end": v(-149.2, 42) * mm});
            skLineSegment(sketch, "E139.MirrorCS", {"start": v(-149.2, -78) * mm, "end": v(-149.2, -66) * mm});
            skLineSegment(sketch, "E140.MirrorCS", {"start": v(-143, -78) * mm, "end": v(-143, -66) * mm});
            skLineSegment(sketch, "E141.MirrorCS", {"start": v(-149.2, -30) * mm, "end": v(-149.2, -18) * mm});
            skLineSegment(sketch, "E142.MirrorCS", {"start": v(-149.2, 54) * mm, "end": v(-143, 54) * mm});
            skLineSegment(sketch, "E143.MirrorCS", {"start": v(-143, -6) * mm, "end": v(-143, -30) * mm, "construction": true});
            skLineSegment(sketch, "E144.MirrorCS", {"start": v(-143, 54) * mm, "end": v(-143, 42) * mm});
            skLineSegment(sketch, "E145.MirrorCS", {"start": v(-143, 6) * mm, "end": v(-143, 30) * mm, "construction": true});
            skLineSegment(sketch, "E146.MirrorCS", {"start": v(-149.2, 78) * mm, "end": v(-143, 78) * mm});
            skLineSegment(sketch, "E147.MirrorCS", {"start": v(-149.2, -78) * mm, "end": v(-143, -78) * mm});
            skLineSegment(sketch, "E148.MirrorCS", {"start": v(-149.2, 90) * mm, "end": v(-143, 90) * mm});
            skLineSegment(sketch, "E149.MirrorCS", {"start": v(-143, 6) * mm, "end": v(-168, 6) * mm, "construction": true});
            skPoint(sketch, "E150.MirrorP", {"position": v(-146.1, 0) * mm});
            skSolve(sketch);
        }
        {
            var Q0;
            Q0=makeQuery(id+"F4.imprint","IMPRINT",FACE,{"disambiguationData":[TD([[makeQuery(id+"F4.imprint","IMPRINT",EDGE,{"derivedFrom":sQuery(id+"F4.wireOp",EDGE,"E96.MirrorCS")}),-1.0]])]});
            var Q1;
            Q1=makeQuery(id+"F4.imprint","IMPRINT",FACE,{"disambiguationData":[TD([[makeQuery(id+"F4.imprint","IMPRINT",EDGE,{"derivedFrom":sQuery(id+"F4.wireOp",EDGE,"E94.MirrorCS")}),1.0]])]});
            var Q2;
            Q2=makeQuery(id+"F4.imprint","IMPRINT",FACE,{"disambiguationData":[TD([[makeQuery(id+"F4.imprint","IMPRINT",EDGE,{"derivedFrom":sQuery(id+"F4.wireOp",EDGE,"E101.MirrorCS")}),1.0]])]});
            var Q3;
            Q3=makeQuery(id+"F4.imprint","IMPRINT",FACE,{"disambiguationData":[TD([[makeQuery(id+"F4.imprint","IMPRINT",EDGE,{"derivedFrom":sQuery(id+"F4.wireOp",EDGE,"E93.MirrorCS")}),1.0]])]});
            var Q4;
            Q4=makeQuery(id+"F4.imprint","IMPRINT",FACE,{"disambiguationData":[TD([[makeQuery(id+"F4.imprint","IMPRINT",EDGE,{"derivedFrom":sQuery(id+"F4.wireOp",EDGE,"E91.bottom")}),1.0]])]});
            var Q5;
            Q5=makeQuery(id+"F4.imprint","IMPRINT",FACE,{"disambiguationData":[TD([[makeQuery(id+"F4.imprint","IMPRINT",EDGE,{"derivedFrom":sQuery(id+"F4.wireOp",EDGE,"E92.0.1.0")}),1.0]])]});
            var Q6;
            Q6=makeQuery(id+"F4.imprint","IMPRINT",FACE,{"disambiguationData":[TD([[makeQuery(id+"F4.imprint","IMPRINT",EDGE,{"derivedFrom":sQuery(id+"F4.wireOp",EDGE,"E92.0.2.0")}),1.0]])]});
            var Q7;
            Q7=makeQuery(id+"F4.imprint","IMPRINT",FACE,{"disambiguationData":[TD([[makeQuery(id+"F4.imprint","IMPRINT",EDGE,{"derivedFrom":sQuery(id+"F4.wireOp",EDGE,"E92.0.3.0")}),1.0]])]});
            var Q8;
            Q8=makeQuery(id+"F4.imprint","IMPRINT",FACE,{"disambiguationData":[TD([[makeQuery(id+"F4.imprint","IMPRINT",EDGE,{"derivedFrom":sQuery(id+"F4.wireOp",EDGE,"E92.0.4.0")}),1.0]])]});
            var Q9;
            Q9=makeQuery(id+"F4.imprint","IMPRINT",FACE,{"disambiguationData":[TD([[makeQuery(id+"F4.imprint","IMPRINT",EDGE,{"derivedFrom":sQuery(id+"F4.wireOp",EDGE,"E123.MirrorCS")}),-1.0]])]});
            var Q10;
            Q10=makeQuery(id+"F4.imprint","IMPRINT",FACE,{"disambiguationData":[TD([[makeQuery(id+"F4.imprint","IMPRINT",EDGE,{"derivedFrom":sQuery(id+"F4.wireOp",EDGE,"E119.MirrorCS")}),1.0]])]});
            var Q11;
            Q11=makeQuery(id+"F4.imprint","IMPRINT",FACE,{"disambiguationData":[TD([[makeQuery(id+"F4.imprint","IMPRINT",EDGE,{"derivedFrom":sQuery(id+"F4.wireOp",EDGE,"E134.MirrorCS")}),1.0]])]});
            var Q12;
            Q12=makeQuery(id+"F4.imprint","IMPRINT",FACE,{"disambiguationData":[TD([[makeQuery(id+"F4.imprint","IMPRINT",EDGE,{"derivedFrom":sQuery(id+"F4.wireOp",EDGE,"E115.MirrorCS")}),-1.0]])]});
            var Q13;
            Q13=makeQuery(id+"F4.imprint","IMPRINT",FACE,{"disambiguationData":[TD([[makeQuery(id+"F4.imprint","IMPRINT",EDGE,{"derivedFrom":sQuery(id+"F4.wireOp",EDGE,"E110.MirrorCS")}),-1.0]])]});
            var Q14;
            Q14=makeQuery(id+"F4.imprint","IMPRINT",FACE,{"disambiguationData":[TD([[makeQuery(id+"F4.imprint","IMPRINT",EDGE,{"derivedFrom":sQuery(id+"F4.wireOp",EDGE,"E116.MirrorCS")}),1.0]])]});
            var Q15;
            Q15=makeQuery(id+"F4.imprint","IMPRINT",FACE,{"disambiguationData":[TD([[makeQuery(id+"F4.imprint","IMPRINT",EDGE,{"derivedFrom":sQuery(id+"F4.wireOp",EDGE,"E120.MirrorCS")}),-1.0]])]});
            var Q16;
            Q16=makeQuery(id+"F4.imprint","IMPRINT",FACE,{"disambiguationData":[TD([[makeQuery(id+"F4.imprint","IMPRINT",EDGE,{"derivedFrom":sQuery(id+"F4.wireOp",EDGE,"E137.MirrorCS")}),-1.0]])]});
            var Q17;
            Q17=makeQuery(id+"F4.imprint","IMPRINT",FACE,{"disambiguationData":[TD([[makeQuery(id+"F4.imprint","IMPRINT",EDGE,{"derivedFrom":sQuery(id+"F4.wireOp",EDGE,"E125.MirrorCS")}),-1.0]])]});
            var Q18;
            {var subQ0=sQuery(id+"F0.wireOp",EDGE,"E0.right");var subQ1=sQuery(id+"F0.wireOp",EDGE,"E0.left");var subQ2=sQuery(id+"F0.wireOp",EDGE,"E0.top");var subQ3=sQuery(id+"F0.wireOp",EDGE,"E0.bottom");Q18=makeQuery(id+"F3.boolean.opBoolean","MERGE",FACE,{"derivedFrom":[makeQuery(id+"F1.opExtrude","CAP_FACE",FACE,{"disambiguationData":[OSD([subQ3,subQ2,subQ1,subQ0])],"isStart":true}),makeQuery(id+"F3.opExtrude","CAP_FACE",FACE,{"disambiguationData":[OSD([subQ3,subQ2,subQ1,subQ0]),OD(0.0)],"isStart":false}),makeQuery(id+"F3.opExtrude","CAP_FACE",FACE,{"disambiguationData":[OSD([subQ3,subQ2,subQ1,subQ0]),OD(1.0)],"isStart":false}),makeQuery(id+"F3.opExtrude","CAP_FACE",FACE,{"disambiguationData":[OSD([subQ3,subQ2,subQ1,subQ0]),OD(2.0)],"isStart":false}),makeQuery(id+"F3.opExtrude","CAP_FACE",FACE,{"disambiguationData":[OSD([subQ3,subQ2,subQ1,subQ0]),OD(3.0)],"isStart":false}),makeQuery(id+"F3.opExtrude","CAP_FACE",FACE,{"disambiguationData":[OSD([subQ3,subQ2,subQ1,subQ0]),OD(4.0)],"isStart":false}),makeQuery(id+"F3.opExtrude","CAP_FACE",FACE,{"disambiguationData":[OSD([subQ3,subQ2,subQ1,subQ0]),OD(5.0)],"isStart":false}),makeQuery(id+"F3.opExtrude","CAP_FACE",FACE,{"disambiguationData":[OSD([subQ3,subQ2,subQ1,subQ0]),OD(6.0)],"isStart":false}),makeQuery(id+"F3.opExtrude","CAP_FACE",FACE,{"disambiguationData":[OSD([subQ3,subQ2,subQ1,subQ0]),OD(7.0)],"isStart":false}),makeQuery(id+"F3.opExtrude","CAP_FACE",FACE,{"disambiguationData":[OSD([subQ3,subQ2,subQ1,subQ0]),OD(8.0)],"isStart":false}),makeQuery(id+"F3.opExtrude","CAP_FACE",FACE,{"disambiguationData":[OSD([subQ3,subQ2,subQ1,subQ0]),OD(9.0)],"isStart":false}),makeQuery(id+"F3.opExtrude","CAP_FACE",FACE,{"disambiguationData":[OSD([subQ3,subQ2,subQ1,subQ0]),OD(10.0)],"isStart":false}),makeQuery(id+"F3.opExtrude","CAP_FACE",FACE,{"disambiguationData":[OSD([subQ3,subQ2,subQ1,subQ0]),OD(11.0)],"isStart":false}),makeQuery(id+"F3.opExtrude","CAP_FACE",FACE,{"disambiguationData":[OSD([subQ3,subQ2,subQ1,subQ0]),OD(12.0)],"isStart":false})]});}
            extrude(context, id + "F5", {"entities" : qUnion([Q0, Q1, Q2, Q3, Q4, Q5, Q6, Q7, Q8, Q9, Q10, Q11, Q12, Q13, Q14, Q15, Q16, Q17]), "operationType" : NewBodyOperationType.ADD, "endBound" : BoundingType.UP_TO_SURFACE, "oppositeDirection" : true, "depth" : 25 * mm, "endBoundEntityFace" : qUnion([Q18]), "offsetDistance" : 25 * mm});
        }
    });
